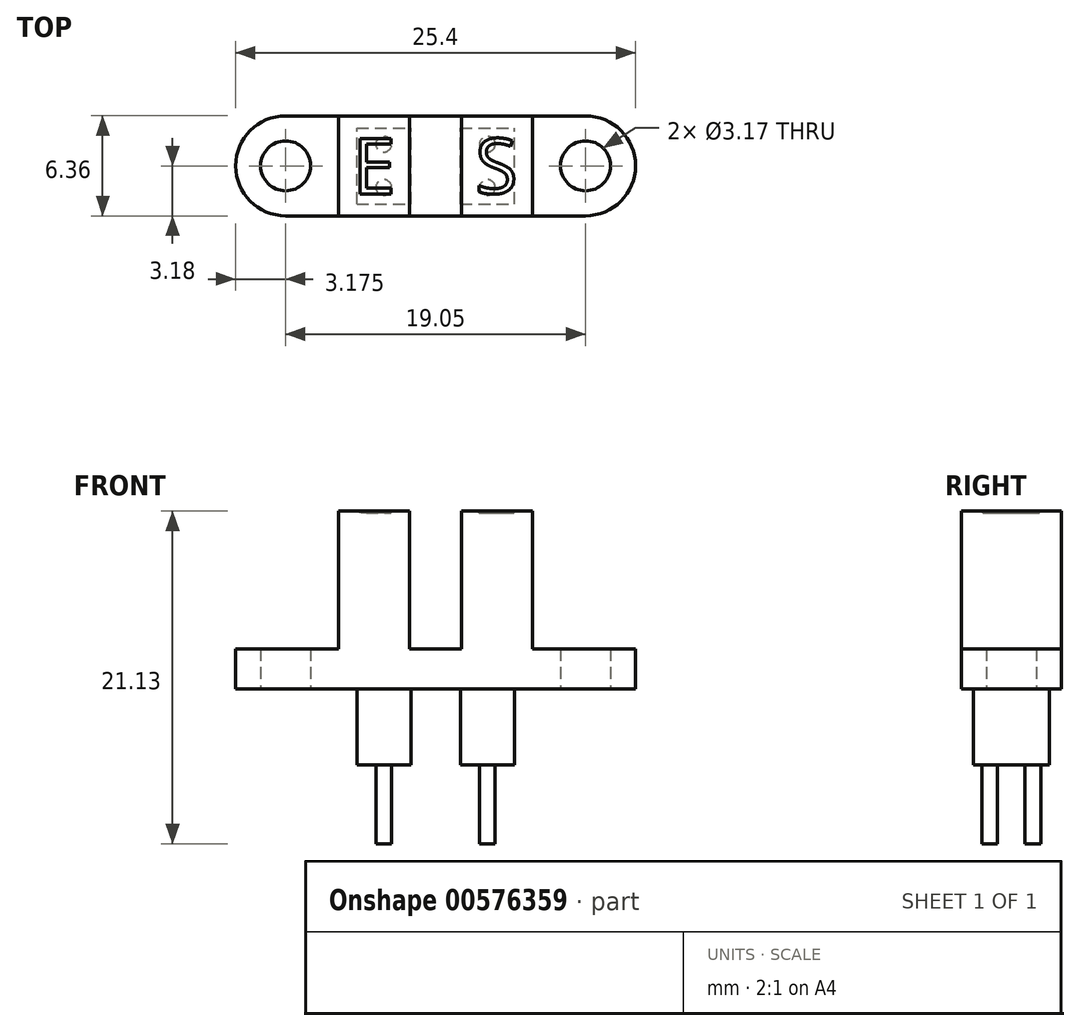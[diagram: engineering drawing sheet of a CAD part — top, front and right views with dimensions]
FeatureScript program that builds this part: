
annotation { "Feature Type Name" : "Feature", "Feature Type Description" : "" }
export const myFeature = defineFeature(function(context is Context, id is Id, definition is map)
    precondition{}
    {
        {
            var Q0;
            Q0=qCreatedBy(makeId("Top.planeOp"),FACE);
            var sketch = newSketch(context, id + "F0", { "sketchPlane" : qUnion([Q0])});
            skLineSegment(sketch, "E0", {"start": v(0, 5.1) * mm, "end": v(0, -6.34) * mm, "construction": true});
            skLineSegment(sketch, "E1", {"start": v(-15.42, 0) * mm, "end": v(15.76, 0) * mm, "construction": true});
            skCircle(sketch, "E2", {"center": v(-9.53, 0) * mm, "radius": 1.59 * mm});
            skCircle(sketch, "E3", {"center": v(9.53, 0) * mm, "radius": 1.59 * mm});
            skArc(sketch, "E4", {"start": v(9.53, -3.17) * mm, "mid": v(12.7, 0) * mm, "end": v(9.53, 3.18) * mm});
            skArc(sketch, "E5", {"start": v(-9.53, 3.18) * mm, "mid": v(-12.7, 0) * mm, "end": v(-9.53, -3.18) * mm});
            skLineSegment(sketch, "E6", {"start": v(-9.53, 3.18) * mm, "end": v(9.53, 3.17) * mm});
            skLineSegment(sketch, "E7", {"start": v(-9.53, -3.18) * mm, "end": v(9.53, -3.17) * mm});
            skSolve(sketch);
        }
        {
            var Q0;
            Q0 = qSketchRegion(id + "F0", true);
            extrude(context, id + "F1", {"entities" : qUnion([Q0]), "depth" : 2.54 * mm, "offsetDistance" : 25 * mm});
        }
        {
            var Q0;
            Q0=makeQuery(id+"F1.opExtrude","CAP_FACE",FACE,{"disambiguationData":[OSD([sQuery(id+"F0.wireOp",EDGE,"E2"),sQuery(id+"F0.wireOp",EDGE,"E3"),sQuery(id+"F0.wireOp",EDGE,"E4"),sQuery(id+"F0.wireOp",EDGE,"E5"),sQuery(id+"F0.wireOp",EDGE,"E6"),sQuery(id+"F0.wireOp",EDGE,"E7")])],"isStart":false});
            var sketch = newSketch(context, id + "F2", { "sketchPlane" : qUnion([Q0])});
            skLineSegment(sketch, "E8.bottom", {"start": v(-6.16, 3.18) * mm, "end": v(-1.65, 3.18) * mm});
            skLineSegment(sketch, "E8.top", {"start": v(-6.16, -3.18) * mm, "end": v(-1.65, -3.18) * mm});
            skLineSegment(sketch, "E8.left", {"start": v(-6.16, 3.18) * mm, "end": v(-6.16, -3.18) * mm});
            skLineSegment(sketch, "E8.right", {"start": v(-1.65, 3.18) * mm, "end": v(-1.65, -3.18) * mm});
            skLineSegment(sketch, "E9.bottom", {"start": v(1.65, 3.18) * mm, "end": v(6.16, 3.18) * mm});
            skLineSegment(sketch, "E9.top", {"start": v(1.65, -3.18) * mm, "end": v(6.16, -3.18) * mm});
            skLineSegment(sketch, "E9.left", {"start": v(1.65, 3.18) * mm, "end": v(1.65, -3.18) * mm});
            skLineSegment(sketch, "E9.right", {"start": v(6.16, 3.18) * mm, "end": v(6.16, -3.18) * mm});
            skSolve(sketch);
        }
        {
            var Q0;
            Q0 = qSketchRegion(id + "F2", true);
            extrude(context, id + "F3", {"entities" : qUnion([Q0]), "operationType" : NewBodyOperationType.ADD, "depth" : 8.76 * mm, "offsetDistance" : 25 * mm});
        }
        {
            var Q0;
            Q0=makeQuery(id+"F3.opExtrude","CAP_FACE",FACE,{"disambiguationData":[OSD([sQuery(id+"F2.wireOp",EDGE,"E8.bottom"),sQuery(id+"F2.wireOp",EDGE,"E8.top"),sQuery(id+"F2.wireOp",EDGE,"E8.left"),sQuery(id+"F2.wireOp",EDGE,"E8.right")])],"isStart":false});
            var sketch = newSketch(context, id + "F4", { "sketchPlane" : qUnion([Q0])});
            skText(sketch, "E10", { "text": "E", "fontName": "OpenSans-Regular.ttf"});
            skText(sketch, "E11", { "text": "S", "fontName": "OpenSans-Regular.ttf"});
            skLineSegment(sketch, "E12", {"start": v(-6.16, -3.18) * mm, "end": v(-1.65, -3.18) * mm, "construction": true});
            skPoint(sketch, "E13", {"position": v(-3.9, -3.18) * mm});
            const initialGuessF4  = {"E10": [-0.00529, -0.00178, 1, 0, 0.00355], "E11": [0.00252, -0.00176, 1, 0, 0.00352]};
            skSetInitialGuess(sketch, initialGuessF4);
            skSolve(sketch);
        }
        {
            var Q0;
            Q0 = qSketchRegion(id + "F4", true);
            extrude(context, id + "F5", {"entities" : qUnion([Q0]), "operationType" : NewBodyOperationType.REMOVE, "oppositeDirection" : true, "depth" : 0.12 * mm, "offsetDistance" : 25 * mm});
        }
        {
            var Q0;
            Q0=makeQuery(id+"F0.imprint","IMPRINT",FACE,{"disambiguationData":[TD([[makeQuery(id+"F0.imprint","IMPRINT",EDGE,{"derivedFrom":sQuery(id+"F0.wireOp",EDGE,"E2")}),-1.0]])]});
            var sketch = newSketch(context, id + "F6", { "sketchPlane" : qUnion([Q0])});
            skLineSegment(sketch, "E14.bottom", {"start": v(-5, -2.41) * mm, "end": v(-1.57, -2.41) * mm});
            skLineSegment(sketch, "E14.top", {"start": v(-5, 2.41) * mm, "end": v(-1.57, 2.41) * mm});
            skLineSegment(sketch, "E14.left", {"start": v(-5, -2.41) * mm, "end": v(-5, 2.41) * mm});
            skLineSegment(sketch, "E14.right", {"start": v(-1.57, -2.41) * mm, "end": v(-1.57, 2.41) * mm});
            skLineSegment(sketch, "E15.bottom", {"start": v(1.57, -2.41) * mm, "end": v(5, -2.41) * mm});
            skLineSegment(sketch, "E15.top", {"start": v(1.57, 2.41) * mm, "end": v(5, 2.41) * mm});
            skLineSegment(sketch, "E15.left", {"start": v(1.57, -2.41) * mm, "end": v(1.57, 2.41) * mm});
            skLineSegment(sketch, "E15.right", {"start": v(5, -2.41) * mm, "end": v(5, 2.41) * mm});
            skSolve(sketch);
        }
        {
            var Q0;
            Q0 = qSketchRegion(id + "F6", true);
            extrude(context, id + "F7", {"entities" : qUnion([Q0]), "operationType" : NewBodyOperationType.ADD, "oppositeDirection" : true, "depth" : 4.83 * mm, "offsetDistance" : 25 * mm});
        }
        {
            var Q0;
            Q0=makeQuery(id+"F7.opExtrude","CAP_FACE",FACE,{"disambiguationData":[OSD([sQuery(id+"F6.wireOp",EDGE,"E14.bottom"),sQuery(id+"F6.wireOp",EDGE,"E14.top"),sQuery(id+"F6.wireOp",EDGE,"E14.left"),sQuery(id+"F6.wireOp",EDGE,"E14.right")])],"isStart":false});
            var sketch = newSketch(context, id + "F8", { "sketchPlane" : qUnion([Q0])});
            skCircle(sketch, "E16", {"center": v(-3.29, 1.38) * mm, "radius": 0.5 * mm});
            skCircle(sketch, "E17", {"center": v(-3.29, -1.38) * mm, "radius": 0.5 * mm});
            skCircle(sketch, "E18", {"center": v(3.29, 1.38) * mm, "radius": 0.5 * mm});
            skCircle(sketch, "E19", {"center": v(3.29, -1.38) * mm, "radius": 0.5 * mm});
            skSolve(sketch);
        }
        {
            var Q0;
            Q0 = qSketchRegion(id + "F8", true);
            extrude(context, id + "F9", {"entities" : qUnion([Q0]), "operationType" : NewBodyOperationType.ADD, "depth" : 5 * mm, "offsetDistance" : 25 * mm});
        }
    });
